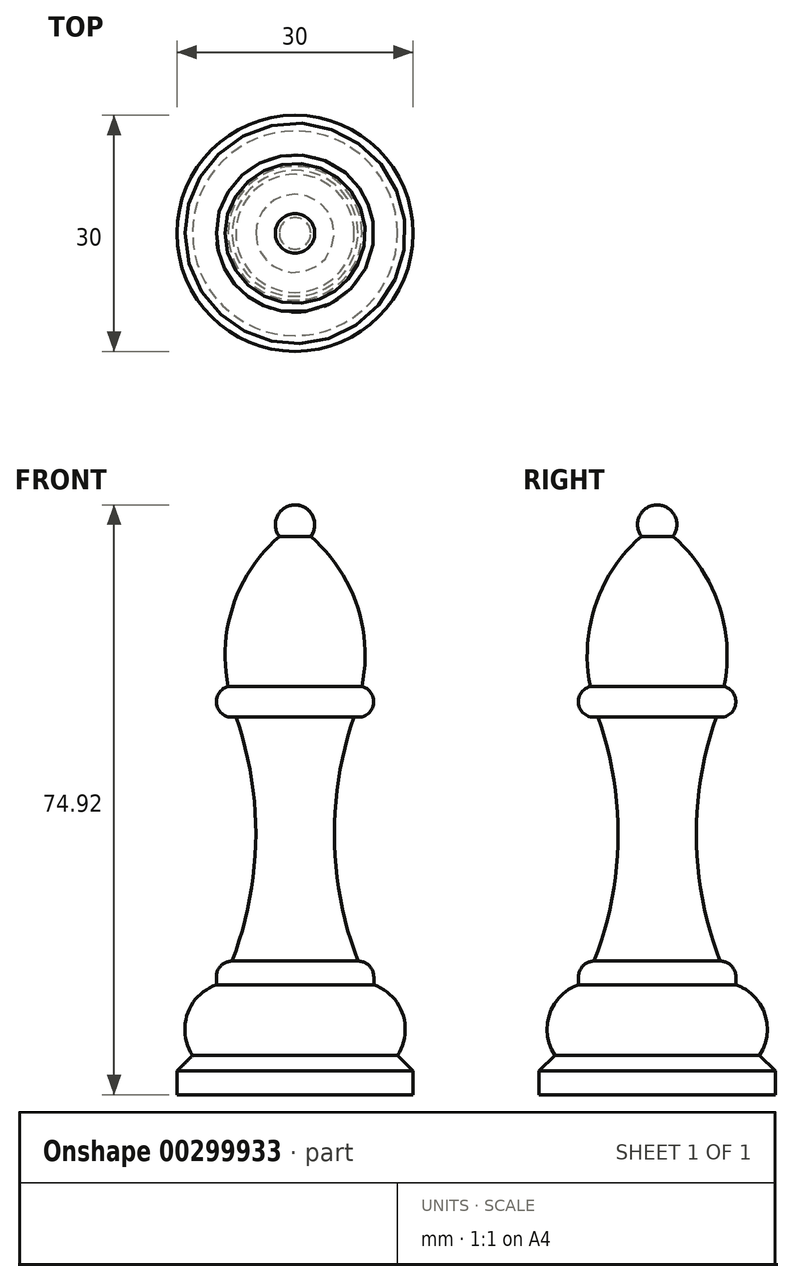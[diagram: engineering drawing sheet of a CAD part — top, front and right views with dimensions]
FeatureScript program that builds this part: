
annotation { "Feature Type Name" : "Feature", "Feature Type Description" : "" }
export const myFeature = defineFeature(function(context is Context, id is Id, definition is map)
    precondition{}
    {
        {
            var Q0;
            Q0=qCreatedBy(makeId("Front.planeOp"),FACE);
            var sketch = newSketch(context, id + "F0", { "sketchPlane" : qUnion([Q0])});
            skArc(sketch, "E0", {"start": v(2, -4) * mm, "mid": v(2.24, -1.38) * mm, "end": v(0, 0) * mm});
            skArc(sketch, "E1", {"start": v(8.5, -23.06) * mm, "mid": v(7.82, -12.65) * mm, "end": v(2, -4) * mm});
            skArc(sketch, "E2", {"start": v(8.5, -26.93) * mm, "mid": v(10, -25) * mm, "end": v(8.5, -23.06) * mm});
            skLineSegment(sketch, "E3", {"start": v(8.5, -26.93) * mm, "end": v(7.5, -26.93) * mm});
            skArc(sketch, "E4", {"start": v(7.5, -26.93) * mm, "mid": v(5, -42.49) * mm, "end": v(8, -57.95) * mm});
            skLineSegment(sketch, "E5", {"start": v(10, -59.95) * mm, "end": v(10, -60.95) * mm});
            skLineSegment(sketch, "E6", {"start": v(13, -69.92) * mm, "end": v(15, -71.92) * mm});
            skLineSegment(sketch, "E7", {"start": v(15, -71.92) * mm, "end": v(15, -74.92) * mm});
            skLineSegment(sketch, "E8", {"start": v(15, -74.92) * mm, "end": v(0, -74.92) * mm});
            skLineSegment(sketch, "E9", {"start": v(0, -74.92) * mm, "end": v(0, 0) * mm});
            skArc(sketch, "E10", {"start": v(13, -69.92) * mm, "mid": v(13.69, -64.7) * mm, "end": v(10, -60.95) * mm});
            skArc(sketch, "E11", {"start": v(10, -59.95) * mm, "mid": v(9.41, -58.54) * mm, "end": v(8, -57.95) * mm});
            skSolve(sketch);
        }
        {
            var Q0;
            Q0=makeQuery(id+"F0.imprint","IMPRINT",FACE,{"disambiguationData":[TD([[makeQuery(id+"F0.imprint","IMPRINT",EDGE,{"derivedFrom":sQuery(id+"F0.wireOp",EDGE,"E0")}),1.0]])]});
            var Q1;
            Q1=sQuery(id+"F0.wireOp",EDGE,"E9");
            revolve(context, id + "F1", {"entities" : qUnion([Q0]), "axis" : qUnion([Q1]), "revolveType" : RevolveType.FULL});
        }
    });
